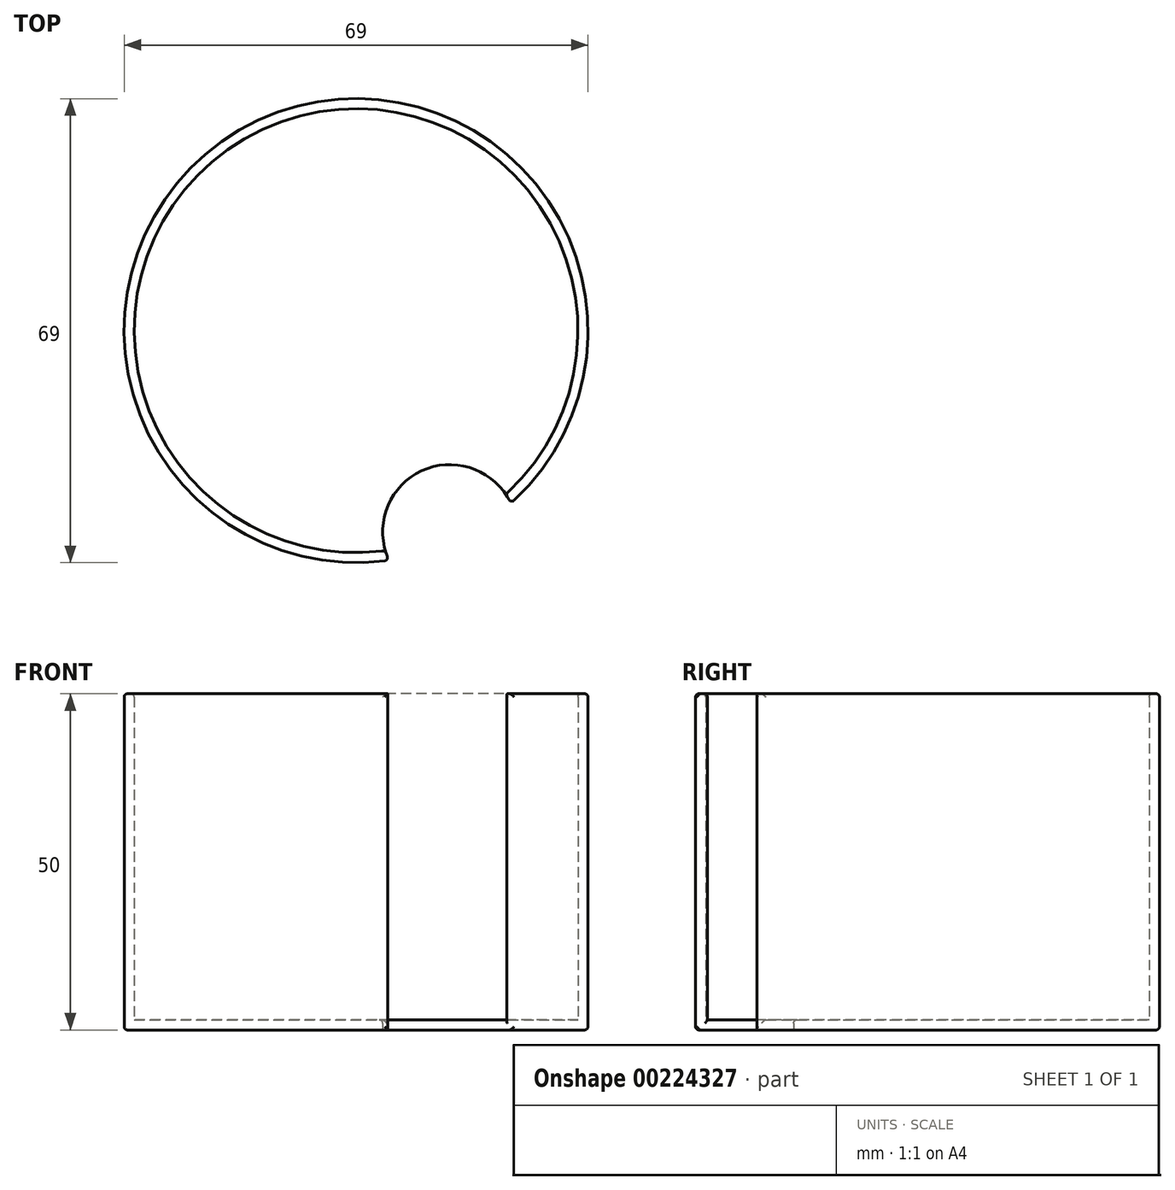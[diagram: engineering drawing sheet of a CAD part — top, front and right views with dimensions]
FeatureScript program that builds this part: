
annotation { "Feature Type Name" : "Feature", "Feature Type Description" : "" }
export const myFeature = defineFeature(function(context is Context, id is Id, definition is map)
    precondition{}
    {
        {
            var Q0;
            Q0=qCreatedBy(makeId("Top.planeOp"),FACE);
            var sketch = newSketch(context, id + "F0", { "sketchPlane" : qUnion([Q0])});
            skCircle(sketch, "E0", {"center": v(-54, 30.6) * mm, "radius": 34.5 * mm});
            skArc(sketch, "E1", {"start": v(-30.97, 4.9) * mm, "mid": v(-44.26, 9.74) * mm, "end": v(-49.1, -3.55) * mm});
            skCircle(sketch, "E2", {"center": v(-54, 30.6) * mm, "radius": 42.5 * mm});
            skSolve(sketch);
        }
        {
            var Q0;
            {var subQ0=sQuery(id+"F0.wireOp",EDGE,"E1");Q0=makeQuery(id+"F0.imprint","IMPRINT",FACE,{"disambiguationData":[TD([[makeQuery(id+"F0.imprint","IMPRINT",EDGE,{"derivedFrom":subQ0}),-1.0]])]});}
            extrude(context, id + "F1", {"entities" : qUnion([Q0]), "depth" : 50 * mm});
        }
        {
            var Q0;
            Q0=makeQuery(id+"F1.opExtrude","CAP_FACE",FACE,{"disambiguationData":[OSD([sQuery(id+"F0.wireOp",EDGE,"E0"),sQuery(id+"F0.wireOp",EDGE,"E1")])],"isStart":false});
            var Q1;
            Q1=makeQuery(id+"F1.opExtrude","SWEPT_FACE",FACE,{"disambiguationData":[OSD([sQuery(id+"F0.wireOp",EDGE,"E1")])]});
            shell(context, id + "F2", {"entities" : qUnion([Q0, Q1]), "thickness" : 1.5 * mm});
        }
        {
            var Q0;
            Q0=makeQuery(id+"F1.opExtrude","CAP_EDGE",EDGE,{"disambiguationData":[OSD([sQuery(id+"F0.wireOp",EDGE,"E0")])],"isStart":false});
            var Q1;
            {var subQ0=sQuery(id+"F0.wireOp",EDGE,"E0");Q1=makeQuery(id+"F2.opShell","OFFSET_EDGE",EDGE,{"disambiguationData":[OSD([subQ0]),TDD([makeQuery(id+"F1.opExtrude","CAP_EDGE",EDGE,{"disambiguationData":[OSD([subQ0])],"isStart":false})])]});}
            var Q2;
            {var subQ0=sQuery(id+"F0.wireOp",EDGE,"E1");var subQ1=sQuery(id+"F0.wireOp",EDGE,"E0");Q2=makeQuery(id+"F2.opShell","OFFSET_EDGE",EDGE,{"disambiguationData":[OSD([subQ1,subQ0]),TDD([makeQuery(id+"F1.opExtrude","SWEPT_EDGE",EDGE,{"disambiguationData":[OSD([subQ1,subQ0]),TDD([makeQuery(id+"F0.imprint","INTERSECT",VERTEX,{"disambiguationData":[OD(0.0)],"derivedFrom":[subQ1,subQ0]})])]})])]});}
            var Q3;
            {var subQ0=sQuery(id+"F0.wireOp",EDGE,"E1");var subQ1=sQuery(id+"F0.wireOp",EDGE,"E0");Q3=makeQuery(id+"F1.opExtrude","SWEPT_EDGE",EDGE,{"disambiguationData":[OSD([subQ1,subQ0]),TDD([makeQuery(id+"F0.imprint","INTERSECT",VERTEX,{"disambiguationData":[OD(0.0)],"derivedFrom":[subQ1,subQ0]})])]});}
            var Q4;
            {var subQ0=sQuery(id+"F0.wireOp",EDGE,"E1");var subQ1=sQuery(id+"F0.wireOp",EDGE,"E0");Q4=makeQuery(id+"F1.opExtrude","SWEPT_EDGE",EDGE,{"disambiguationData":[OSD([subQ1,subQ0]),TDD([makeQuery(id+"F0.imprint","INTERSECT",VERTEX,{"disambiguationData":[OD(1.0)],"derivedFrom":[subQ1,subQ0]})])]});}
            var Q5;
            {var subQ0=sQuery(id+"F0.wireOp",EDGE,"E1");var subQ1=sQuery(id+"F0.wireOp",EDGE,"E0");Q5=makeQuery(id+"F2.opShell","OFFSET_EDGE",EDGE,{"disambiguationData":[OSD([subQ1,subQ0]),TDD([makeQuery(id+"F1.opExtrude","SWEPT_EDGE",EDGE,{"disambiguationData":[OSD([subQ1,subQ0]),TDD([makeQuery(id+"F0.imprint","INTERSECT",VERTEX,{"disambiguationData":[OD(1.0)],"derivedFrom":[subQ1,subQ0]})])]})])]});}
            var Q6;
            {var subQ0=sQuery(id+"F0.wireOp",EDGE,"E1");Q6=makeQuery(id+"F2.opShell","OFFSET_EDGE",EDGE,{"disambiguationData":[OSD([subQ0]),TDD([makeQuery(id+"F1.opExtrude","CAP_EDGE",EDGE,{"disambiguationData":[OSD([subQ0])],"isStart":true})])]});}
            var Q7;
            Q7=makeQuery(id+"F1.opExtrude","CAP_EDGE",EDGE,{"disambiguationData":[OSD([sQuery(id+"F0.wireOp",EDGE,"E0")])],"isStart":true});
            fillet(context, id + "F3", {"entities" : qUnion([Q0, Q1, Q2, Q3, Q4, Q5, Q6, Q7]), "radius" : 0.5 * mm, "tangentPropagation" : true, "allowEdgeOverflow" : false});
        }
    });
